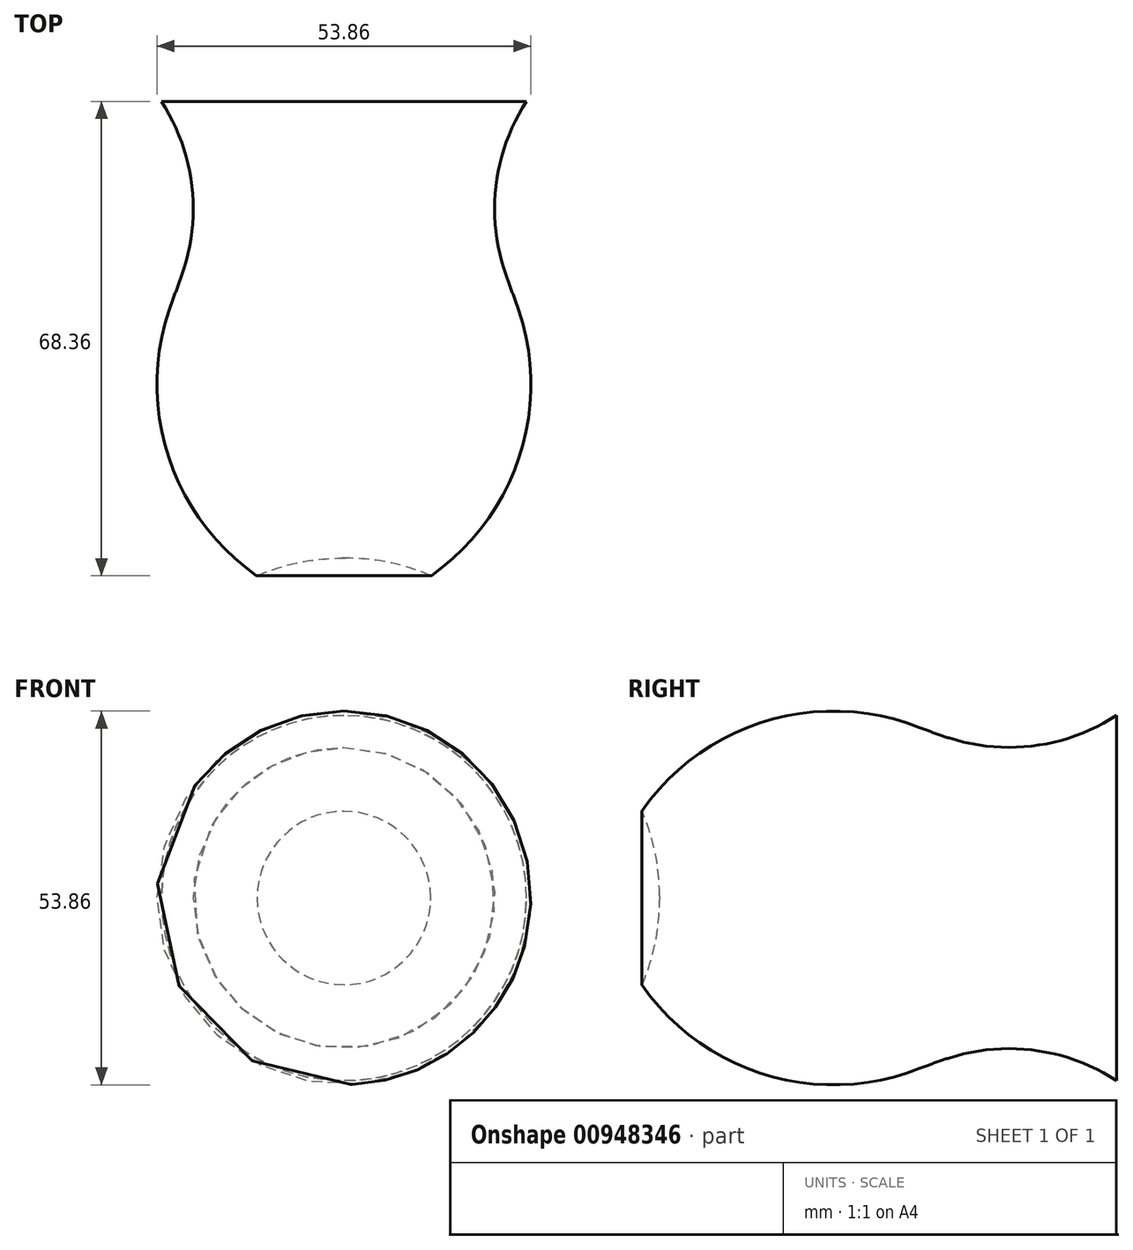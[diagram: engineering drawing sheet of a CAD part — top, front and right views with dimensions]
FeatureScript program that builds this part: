
annotation { "Feature Type Name" : "Feature", "Feature Type Description" : "" }
export const myFeature = defineFeature(function(context is Context, id is Id, definition is map)
    precondition{}
    {
        {
            var Q0;
            Q0=qCreatedBy(makeId("Top.planeOp"),FACE);
            var sketch = newSketch(context, id + "F0", { "sketchPlane" : qUnion([Q0])});
            skLineSegment(sketch, "E0", {"start": v(0, 40.38) * mm, "end": v(26.32, 40.38) * mm});
            skLineSegment(sketch, "E1", {"start": v(0, -27.98) * mm, "end": v(12.57, -27.98) * mm});
            skArc(sketch, "E2", {"start": v(12.57, -27.98) * mm, "mid": v(25.51, -10.05) * mm, "end": v(24.57, 12.05) * mm});
            skArc(sketch, "E3", {"start": v(23.05, 16.29) * mm, "mid": v(23.78, 14.16) * mm, "end": v(24.57, 12.05) * mm});
            skArc(sketch, "E4", {"start": v(26.32, 40.38) * mm, "mid": v(21.96, 28.7) * mm, "end": v(23.05, 16.29) * mm});
            skLineSegment(sketch, "E5", {"start": v(0, 40.38) * mm, "end": v(0, -27.98) * mm});
            skPoint(sketch, "E6.visualSharp", {"position": v(23.05, 16.29) * mm});
            skLineSegment(sketch, "E6.filletArc", {"start": v(23.05, 16.29) * mm, "end": v(23.05, 16.29) * mm});
            skSolve(sketch);
        }
        {
            var Q0;
            Q0=makeQuery(id+"F0.imprint","IMPRINT",FACE,{"disambiguationData":[TD([[makeQuery(id+"F0.imprint","IMPRINT",EDGE,{"derivedFrom":sQuery(id+"F0.wireOp",EDGE,"E0")}),-1.0]])]});
            var Q1;
            Q1=sQuery(id+"F0.wireOp",EDGE,"E5");
            revolve(context, id + "F1", {"surfaceOperationType" : NewSurfaceOperationType.NEW, "entities" : qUnion([Q0]), "axis" : qUnion([Q1]), "revolveType" : RevolveType.FULL});
        }
        {
            var Q0;
            Q0=makeQuery(id+"F1.opRevolve","SWEPT_EDGE",EDGE,{"disambiguationData":[OSD([sQuery(id+"F0.wireOp",EDGE,"E1"),sQuery(id+"F0.wireOp",EDGE,"E2")])]});
            fillet(context, id + "F2", {"entities" : qUnion([Q0]), "radius" : 0.2 * mm, "tangentPropagation" : true, "allowEdgeOverflow" : false});
        }
        {
            var Q0;
            Q0=makeQuery(id+"F1.opRevolve","SWEPT_FACE",FACE,{"disambiguationData":[OSD([sQuery(id+"F0.wireOp",EDGE,"E0")])]});
            shell(context, id + "F3", {"entities" : qUnion([Q0]), "thickness" : 0.03 * mm});
        }
        {
            var Q0;
            Q0=makeQuery(id+"F1.opRevolve","SWEPT_FACE",FACE,{"disambiguationData":[OSD([sQuery(id+"F0.wireOp",EDGE,"E1")])]});
            extrude(context, id + "F4", {"entities" : qUnion([Q0]), "operationType" : NewBodyOperationType.ADD, "depth" : -2.54 * mm, "offsetDistance" : 25.4 * mm});
        }
        {
            var Q0;
            Q0=makeQuery(id+"F4.opExtrude","CAP_FACE",FACE,{"disambiguationData":[OSD([sQuery(id+"F0.wireOp",EDGE,"E1")])],"isStart":false});
            fillet(context, id + "F5", {"entities" : qUnion([Q0]), "radius" : 30.66 * mm, "tangentPropagation" : true, "allowEdgeOverflow" : false});
        }
    });
